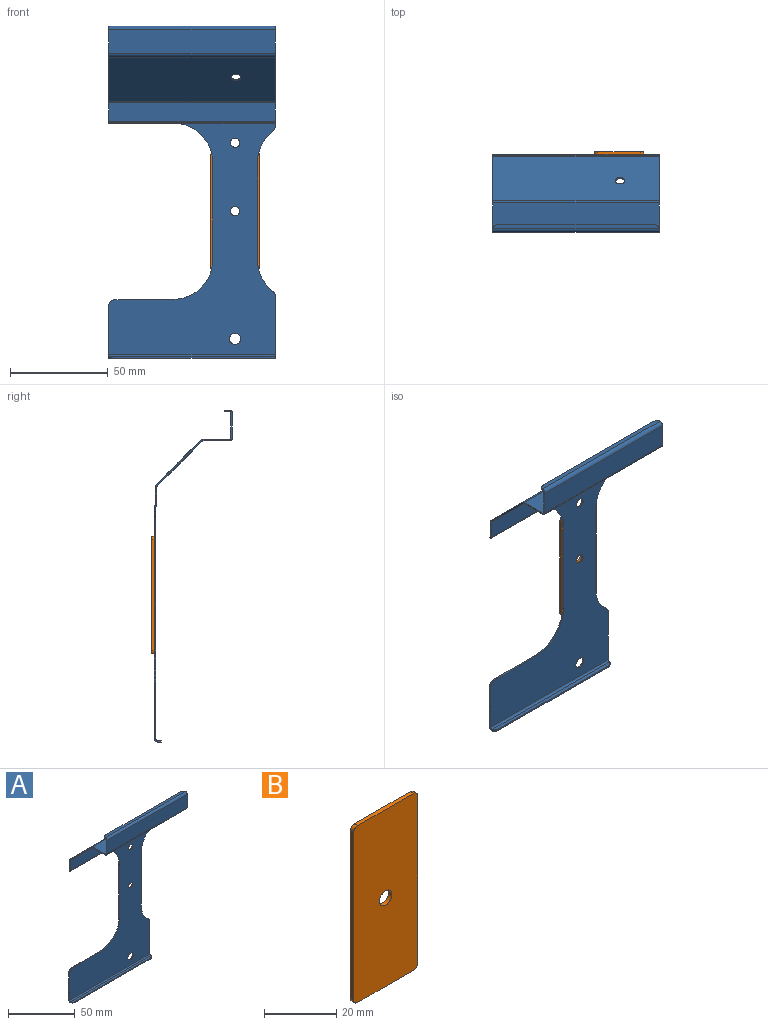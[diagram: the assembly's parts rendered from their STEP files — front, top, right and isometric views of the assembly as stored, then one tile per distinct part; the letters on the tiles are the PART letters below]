
ASSEMBLY  parts=2 mates=1
PART A: 78 faces, bbox 85x40.1x169.6 mm
  f0: plane 51.4x0.81mm, normal (1,0,0), area 41.8mm2, adj f1,f12,f13,f14
  f1: cylinder r=20mm len=15.12mm, axis (0,1,0), area 14.3mm2, adj f0,f13,f14,f15
  f2: plane 29.85x0.81mm, normal (1,0,0), area 24.3mm2, adj f13,f14,f15,f31
  f3: plane 24.74x0.81mm, normal (-1,0,0), area 20.1mm2, adj f13,f14,f16,f32
  f4: plane 30.03x0.81mm, normal (-0.01,0,1), area 24.4mm2, adj f5,f13,f14,f16
  f5: cylinder r=20mm len=20mm, axis (0,1,0), area 25.4mm2, adj f4,f6,f13,f14
  f6: plane 50.23x0.81mm, normal (-1,0,0), area 40.8mm2, adj f5,f7,f13,f14
  f7: cylinder r=20mm len=19.76mm, axis (0,1,0), area 24.8mm2, adj f6,f13,f14,f23
  f8: plane 1.65x0.81mm, normal (1,0,0), area 1.3mm2, adj f13,f14,f17,f24
  f9: cylinder r=2.9mm len=5.79mm, axis (0,1,0), area 14.8mm2, adj f13,f14
  f10: cylinder r=2.38mm len=4.76mm, axis (0,1,0), area 12.2mm2, adj f13,f14
  f11: cylinder r=2.38mm len=4.76mm, axis (0,1,0), area 12.2mm2, adj f13,f14
  f12: cylinder r=20mm len=15.12mm, axis (0,1,0), area 14.3mm2, adj f0,f13,f14,f17
  f13: plane 118.17x85mm, normal (0,1,0), area 4716.2mm2, adj f0,f1,f2,f3,f4,f5,f6,f7
  f14: plane 118.17x85mm, normal (0,-1,0), area 4716.2mm2, adj f0,f1,f2,f3,f4,f5,f6,f7
  f15: cylinder r=3.17mm len=2.51mm, axis (0,1,0), area 2.4mm2, adj f1,f2,f13,f14
  f16: cylinder r=3.17mm len=3.18mm, axis (0,-1,0), area 4mm2, adj f3,f4,f13,f14
  f17: cylinder r=3.17mm len=2.51mm, axis (0,1,0), area 2.4mm2, adj f8,f12,f13,f14
  f18: plane 1.03x1.03mm, normal (1,0,0), area 0.5mm2, adj f21,f22,f24,f27
  f19: plane 33.73x0.57mm, normal (0,0.71,-0.71), area 27.4mm2, adj f20,f21,f22,f23
  f20: plane 1.03x1.03mm, normal (-1,0,0), area 0.5mm2, adj f19,f21,f22,f28
  f21: plane 85x0.45mm, normal (0,0.71,0.71), area 54.1mm2, adj f18,f19,f20,f25,f30
  f22: plane 85x0.45mm, normal (0,-0.71,-0.71), area 54.1mm2, adj f18,f19,f20,f26,f29
  f23: plane 0.82x0.6mm, normal (-1,0,0), area 0.3mm2, adj f7,f19,f25,f26
  f24: plane 0.82x0.6mm, normal (1,0,0), area 0.3mm2, adj f8,f18,f25,f26
  f25: cylinder r=0.84mm len=51.27mm, axis (-1,0,0), area 34mm2, adj f13,f21,f23,f24
  f26: cylinder r=0.03mm len=51.27mm, axis (-1,0,0), area 1.3mm2, adj f14,f22,f23,f24
  f27: plane 0.82x0.6mm, normal (1,0,0), area 0.3mm2, adj f18,f29,f30,f40
  f28: plane 0.82x0.6mm, normal (-1,0,0), area 0.3mm2, adj f20,f29,f30,f41
  f29: cylinder r=0.84mm len=85mm, axis (1,0,0), area 56.4mm2, adj f22,f27,f28,f43
  f30: cylinder r=0.03mm len=85mm, axis (1,0,0), area 2.1mm2, adj f21,f27,f28,f42
  f31: plane 1.81x1.81mm, normal (1,0,0), area 1.8mm2, adj f2,f33,f34,f39
  f32: plane 1.81x1.81mm, normal (-1,0,0), area 1.8mm2, adj f3,f33,f34,f38
  f33: cylinder r=1.81mm len=85mm, axis (1,0,0), area 242mm2, adj f13,f31,f32,f36
  f34: cylinder r=1mm len=85mm, axis (1,0,0), area 133.5mm2, adj f14,f31,f32,f37
  f35: plane 79.1x0.81mm, normal (0,-1,0), area 64.3mm2, adj f36,f37,f38,f39
  f36: plane 85x2mm, normal (0,0,-1), area 166.7mm2, adj f33,f35,f38,f39
  f37: plane 85x2mm, normal (0,0,1), area 166.7mm2, adj f34,f35,f38,f39
  f38: cylinder r=3.17mm len=2.95mm, axis (0,0,-1), area 3.1mm2, adj f32,f35,f36,f37
  f39: cylinder r=3.17mm len=2.95mm, axis (0,0,-1), area 3.1mm2, adj f31,f35,f36,f37
  f40: plane 9.24x0.81mm, normal (1,0,0), area 7.5mm2, adj f27,f42,f43,f45
  f41: plane 9.24x0.81mm, normal (-1,0,0), area 7.5mm2, adj f28,f42,f43,f44
  f42: plane 85x9.24mm, normal (0,1,0), area 785mm2, adj f30,f40,f41,f46
  f43: plane 85x9.24mm, normal (0,-1,0), area 785mm2, adj f29,f40,f41,f47
  f44: plane 1.28x1.11mm, normal (-1,0,0), area 0.9mm2, adj f41,f46,f47,f50
  f45: plane 1.28x1.11mm, normal (1,0,0), area 0.9mm2, adj f40,f46,f47,f48
  f46: cylinder r=1.81mm len=85mm, axis (-1,0,0), area 121mm2, adj f42,f44,f45,f51
  f47: cylinder r=1mm len=85mm, axis (-1,0,0), area 66.8mm2, adj f43,f44,f45,f52
  f48: plane 23.09x23.09mm, normal (1,0,0), area 25.9mm2, adj f45,f51,f52,f54
  f49: cylinder r=2.38mm len=4.76mm, axis (0,0.71,0.71), area 12.2mm2, adj f51,f52
  f50: plane 23.09x23.09mm, normal (-1,0,0), area 25.9mm2, adj f44,f51,f52,f53
  f51: plane 85x22.51mm, normal (0,0.71,0.71), area 2688.2mm2, adj f46,f48,f49,f50,f55
  f52: plane 85x22.51mm, normal (0,-0.71,-0.71), area 2688.2mm2, adj f47,f48,f49,f50,f56
  f53: plane 1.28x1.11mm, normal (-1,0,0), area 0.9mm2, adj f50,f55,f56,f58
  f54: plane 1.28x1.11mm, normal (1,0,0), area 0.9mm2, adj f48,f55,f56,f57
  f55: cylinder r=1.81mm len=85mm, axis (-1,0,0), area 121mm2, adj f51,f53,f54,f59
  f56: cylinder r=1mm len=85mm, axis (-1,0,0), area 66.8mm2, adj f52,f53,f54,f60
  f57: plane 13.25x0.81mm, normal (1,0,0), area 10.8mm2, adj f54,f59,f60,f61
  f58: plane 13.25x0.81mm, normal (-1,0,0), area 10.8mm2, adj f53,f59,f60,f62
  f59: plane 85x13.25mm, normal (0,0,1), area 1126.2mm2, adj f55,f57,f58,f64
  f60: plane 85x13.25mm, normal (0,0,-1), area 1126.2mm2, adj f56,f57,f58,f63
  f61: plane 1.81x1.81mm, normal (1,0,0), area 1.8mm2, adj f57,f63,f64,f65
  f62: plane 1.81x1.81mm, normal (-1,0,0), area 1.8mm2, adj f58,f63,f64,f66
  f63: cylinder r=1.81mm len=85mm, axis (1,0,0), area 242mm2, adj f60,f61,f62,f68
  f64: cylinder r=1mm len=85mm, axis (1,0,0), area 133.5mm2, adj f59,f61,f62,f67
  f65: plane 12.19x0.81mm, normal (1,0,0), area 9.9mm2, adj f61,f67,f68,f74
  f66: plane 12.19x0.81mm, normal (-1,0,0), area 9.9mm2, adj f62,f67,f68,f75
  f67: plane 85x12.19mm, normal (0,1,0), area 1035.9mm2, adj f64,f65,f66,f77
  f68: plane 85x12.19mm, normal (0,-1,0), area 1035.9mm2, adj f63,f65,f66,f76
  f69: plane 78.97x0.81mm, normal (0,1,0), area 64.2mm2, adj f70,f71,f72,f73
  f70: plane 85x2.19mm, normal (0,0,-1), area 182.4mm2, adj f69,f72,f73,f77
  f71: plane 85x2.19mm, normal (0,0,1), area 182.4mm2, adj f69,f72,f73,f76
  f72: cylinder r=3.17mm len=3.02mm, axis (0,0,1), area 3.2mm2, adj f69,f70,f71,f75
  f73: cylinder r=3.17mm len=3.02mm, axis (0,0,-1), area 3.2mm2, adj f69,f70,f71,f74
  f74: plane 1.81x1.81mm, normal (1,0,0), area 1.8mm2, adj f65,f73,f76,f77
  f75: plane 1.81x1.81mm, normal (-1,0,0), area 1.8mm2, adj f66,f72,f76,f77
  f76: cylinder r=1.81mm len=85mm, axis (1,0,0), area 242mm2, adj f68,f71,f74,f75
  f77: cylinder r=1mm len=85mm, axis (1,0,0), area 133.5mm2, adj f67,f70,f74,f75
PART B: 11 faces, bbox 25x1.3x60 mm
  f0: plane 56.83x1.27mm, normal (1,0,0), area 72.2mm2, adj f1,f7,f8,f9
  f1: cylinder r=1.59mm len=1.59mm, axis (0,1,0), area 3.2mm2, adj f0,f2,f8,f9
  f2: plane 21.83x1.27mm, normal (0,0,1), area 27.7mm2, adj f1,f3,f8,f9
  f3: cylinder r=1.59mm len=1.59mm, axis (0,1,0), area 3.2mm2, adj f2,f4,f8,f9
  f4: plane 56.83x1.27mm, normal (-1,0,0), area 72.2mm2, adj f3,f5,f8,f9
  f5: cylinder r=1.59mm len=1.59mm, axis (0,1,0), area 3.2mm2, adj f4,f6,f8,f9
  f6: plane 21.83x1.27mm, normal (0,0,-1), area 27.7mm2, adj f5,f7,f8,f9
  f7: cylinder r=1.59mm len=1.59mm, axis (0,1,0), area 3.2mm2, adj f0,f6,f8,f9
  f8: plane 60x25mm, normal (0,-1,0), area 1479.4mm2, adj f0,f1,f2,f3,f4,f5,f6,f7
  f9: plane 60x25mm, normal (0,1,0), area 1479.4mm2, adj f0,f1,f2,f3,f4,f5,f6,f7
  f10: cylinder r=2.43mm len=4.85mm, axis (0,1,0), area 19.4mm2, adj f8,f9
PLACE A t=(-22.04,-0.32,-74.97)mm
PLACE B t=(-0.02,1.77,0.03)mm
MATE fastened B.f10 <-> A.f11  axis (0,-1,0) through (-0.02,0.5,0.03)mm
